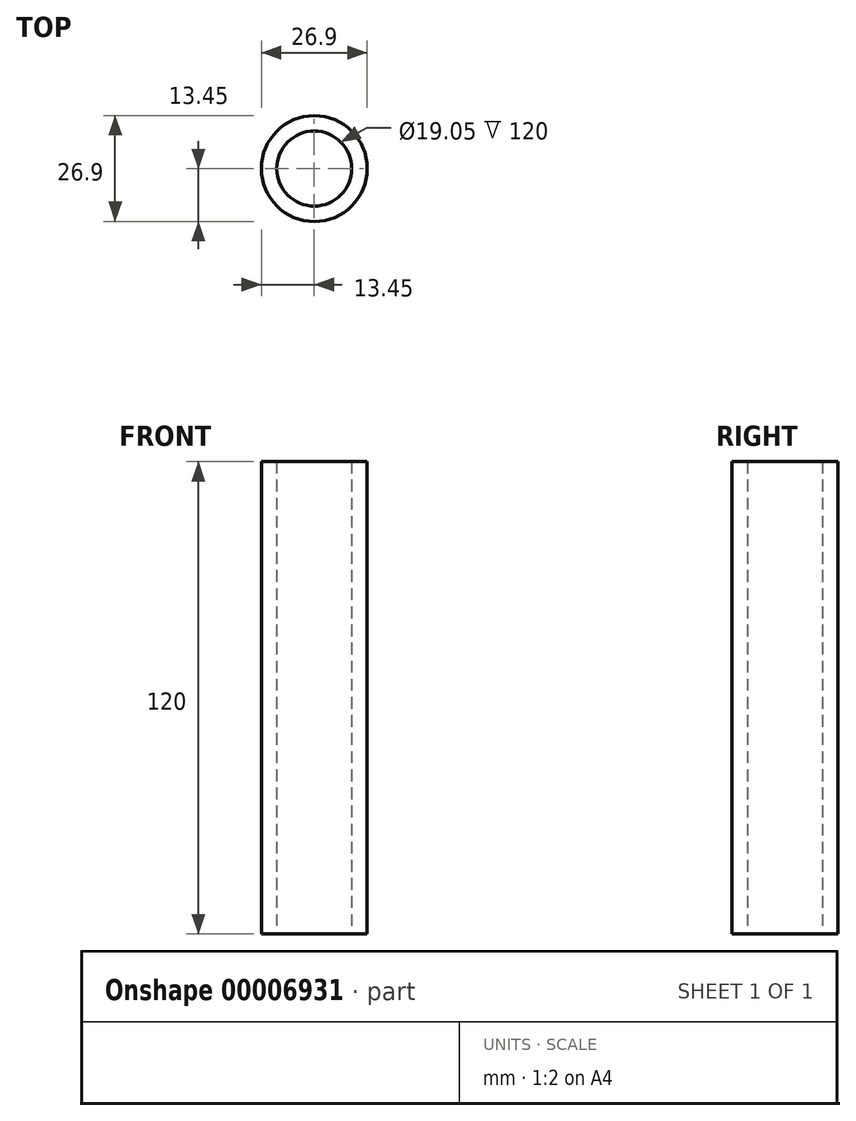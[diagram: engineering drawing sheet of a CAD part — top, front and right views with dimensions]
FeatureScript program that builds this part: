
annotation { "Feature Type Name" : "Feature", "Feature Type Description" : "" }
export const myFeature = defineFeature(function(context is Context, id is Id, definition is map)
    precondition{}
    {
        {
            var Q0;
            Q0=qCreatedBy(makeId("Top.planeOp"),FACE);
            var sketch = newSketch(context, id + "F0", { "sketchPlane" : qUnion([Q0])});
            skCircle(sketch, "E0", {"center": v(0, 0) * mm, "radius": 13.45 * mm});
            skCircle(sketch, "E1", {"center": v(0, 0) * mm, "radius": 9.53 * mm});
            skSolve(sketch);
        }
        {
            var Q0;
            Q0=makeQuery(id+"F0.imprint","IMPRINT",FACE,{"disambiguationData":[TD([[makeQuery(id+"F0.imprint","IMPRINT",EDGE,{"derivedFrom":sQuery(id+"F0.wireOp",EDGE,"E0")}),1.0]])]});
            extrude(context, id + "F1", {"entities" : qUnion([Q0]), "depth" : 120 * mm});
        }
    });
